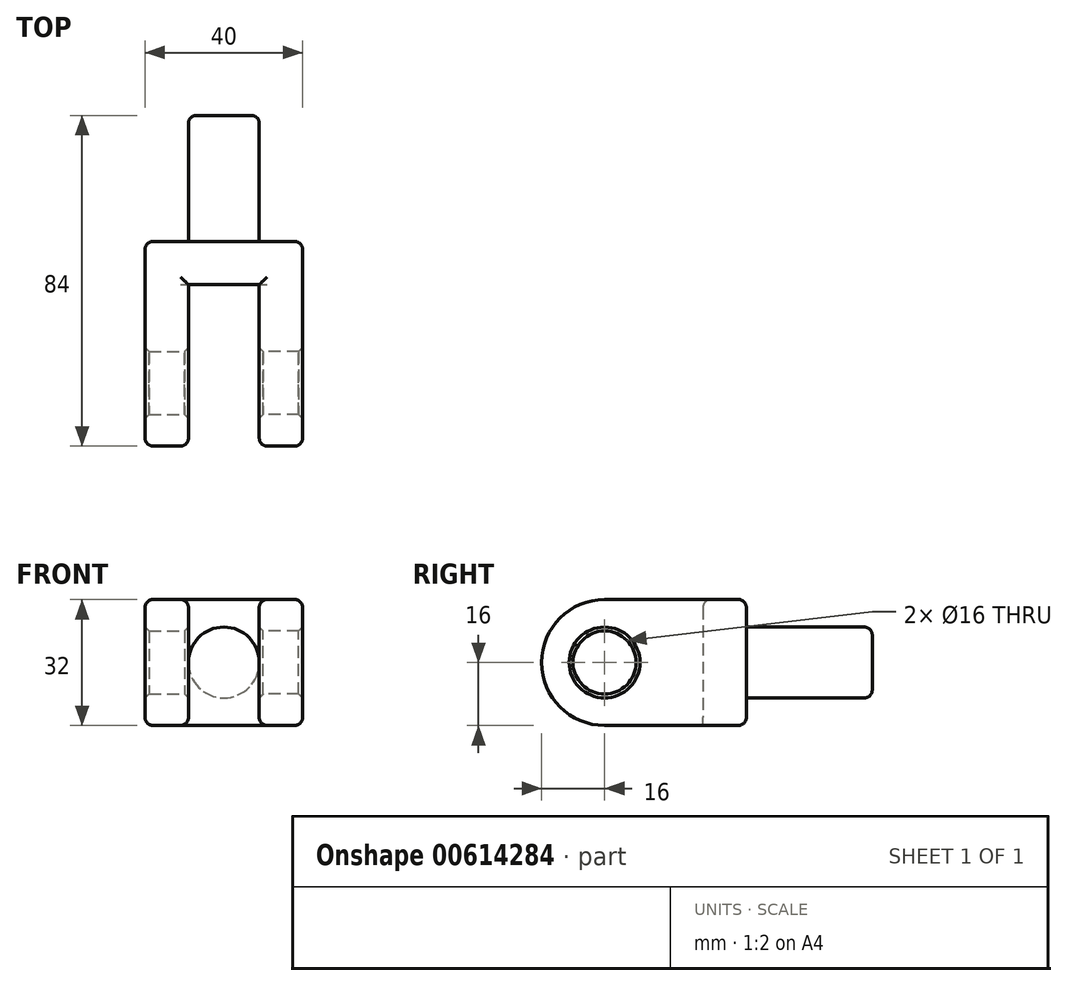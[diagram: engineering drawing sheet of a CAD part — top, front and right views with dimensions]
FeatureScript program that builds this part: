
annotation { "Feature Type Name" : "Feature", "Feature Type Description" : "" }
export const myFeature = defineFeature(function(context is Context, id is Id, definition is map)
    precondition{}
    {
        {
            var Q0;
            Q0=qCreatedBy(makeId("Front.planeOp"),FACE);
            var sketch = newSketch(context, id + "F0", { "sketchPlane" : qUnion([Q0])});
            skLineSegment(sketch, "E0.bottom", {"start": v(-9, 16) * mm, "end": v(9, 16) * mm});
            skLineSegment(sketch, "E0.top", {"start": v(-9, -16) * mm, "end": v(9, -16) * mm});
            skLineSegment(sketch, "E0.left", {"start": v(-9, 16) * mm, "end": v(-9, -16) * mm});
            skLineSegment(sketch, "E0.right", {"start": v(9, 16) * mm, "end": v(9, -16) * mm});
            skSolve(sketch);
        }
        {
            var Q0;
            Q0 = qSketchRegion(id + "F0", true);
            extrude(context, id + "F1", {"entities" : qUnion([Q0]), "depth" : 11 * mm, "offsetDistance" : 25 * mm});
        }
        {
            var Q0;
            Q0=makeQuery(id+"F1.opExtrude","SWEPT_FACE",FACE,{"disambiguationData":[OSD([sQuery(id+"F0.wireOp",EDGE,"E0.right")])]});
            var sketch = newSketch(context, id + "F2", { "sketchPlane" : qUnion([Q0])});
            skLineSegment(sketch, "E1", {"start": v(0, -16) * mm, "end": v(0, 16) * mm});
            skLineSegment(sketch, "E2", {"start": v(0, 16) * mm, "end": v(-36, 16) * mm});
            skPoint(sketch, "E2.endSnap0", {"position": v(-5.5, 16) * mm});
            skLineSegment(sketch, "E3", {"start": v(0, -16) * mm, "end": v(-36, -16) * mm});
            skArc(sketch, "E4", {"start": v(-36, 16) * mm, "mid": v(-52, 0) * mm, "end": v(-36, -16) * mm});
            skCircle(sketch, "E5", {"center": v(-36, 0) * mm, "radius": 8 * mm});
            skSolve(sketch);
        }
        {
            var Q0;
            Q0 = qSketchRegion(id + "F2", true);
            extrude(context, id + "F3", {"entities" : qUnion([Q0]), "operationType" : NewBodyOperationType.ADD, "depth" : 11 * mm, "offsetDistance" : 25 * mm});
        }
        {
            var Q0;
            Q0=makeQuery(id+"F1.opExtrude","SWEPT_BODY",BODY,{"disambiguationData":[OSD([sQuery(id+"F0.wireOp",EDGE,"E0.bottom"),sQuery(id+"F0.wireOp",EDGE,"E0.top"),sQuery(id+"F0.wireOp",EDGE,"E0.left"),sQuery(id+"F0.wireOp",EDGE,"E0.right")])]});
            var Q1;
            Q1=qCreatedBy(makeId("Right.planeOp"),FACE);
            mirror(context, id + "F4", {"operationType" : NewBodyOperationType.ADD, "entities" : qUnion([Q0]), "mirrorPlane" : qUnion([Q1])});
        }
        {
            var Q0;
            {var subQ0=makeQuery(id+"F3.boolean.opBoolean","MERGE",FACE,{"derivedFrom":[makeQuery(id+"F1.opExtrude","CAP_FACE",FACE,{"disambiguationData":[OSD([sQuery(id+"F0.wireOp",EDGE,"E0.bottom"),sQuery(id+"F0.wireOp",EDGE,"E0.top"),sQuery(id+"F0.wireOp",EDGE,"E0.left"),sQuery(id+"F0.wireOp",EDGE,"E0.right")])],"isStart":true}),makeQuery(id+"F3.opExtrude","SWEPT_FACE",FACE,{"disambiguationData":[OSD([sQuery(id+"F2.wireOp",EDGE,"E1")])]})]});Q0=makeQuery(id+"F4.boolean.opBoolean","MERGE",FACE,{"derivedFrom":[subQ0,makeQuery(id+"F4.opPattern","COPY",FACE,{"derivedFrom":subQ0,"instanceName":"1"})]});}
            var sketch = newSketch(context, id + "F5", { "sketchPlane" : qUnion([Q0])});
            skCircle(sketch, "E6", {"center": v(0, 0) * mm, "radius": 9 * mm});
            skSolve(sketch);
        }
        {
            var Q0;
            Q0=makeQuery(id+"F5.imprint","IMPRINT",FACE,{"disambiguationData":[TD([[makeQuery(id+"F5.imprint","IMPRINT",EDGE,{"derivedFrom":sQuery(id+"F5.wireOp",EDGE,"E6")}),1.0]])]});
            extrude(context, id + "F6", {"entities" : qUnion([Q0]), "operationType" : NewBodyOperationType.ADD, "depth" : 32 * mm, "offsetDistance" : 25 * mm});
        }
        {
            var Q0;
            Q0=makeQuery(id+"F3.opExtrude","CAP_EDGE",EDGE,{"disambiguationData":[OSD([sQuery(id+"F2.wireOp",EDGE,"E5")])],"isStart":true});
            var Q1;
            Q1=makeQuery(id+"F3.opExtrude","CAP_EDGE",EDGE,{"disambiguationData":[OSD([sQuery(id+"F2.wireOp",EDGE,"E5")])],"isStart":false});
            var Q2;
            Q2=makeQuery(id+"F4.opPattern","COPY",EDGE,{"derivedFrom":makeQuery(id+"F3.opExtrude","CAP_EDGE",EDGE,{"disambiguationData":[OSD([sQuery(id+"F2.wireOp",EDGE,"E5")])],"isStart":true}),"instanceName":"1"});
            var Q3;
            Q3=makeQuery(id+"F4.opPattern","COPY",EDGE,{"derivedFrom":makeQuery(id+"F3.opExtrude","CAP_EDGE",EDGE,{"disambiguationData":[OSD([sQuery(id+"F2.wireOp",EDGE,"E5")])],"isStart":false}),"instanceName":"1"});
            chamfer(context, id + "F7", {"entities" : qUnion([Q0, Q1, Q2, Q3]), "width" : 1 * mm, "tangentPropagation" : true});
        }
        {
            var Q0;
            {var subQ0=makeQuery(id+"F3.boolean.opBoolean","MERGE",FACE,{"derivedFrom":[makeQuery(id+"F1.opExtrude","SWEPT_FACE",FACE,{"disambiguationData":[OSD([sQuery(id+"F0.wireOp",EDGE,"E0.bottom")])]}),makeQuery(id+"F3.opExtrude","SWEPT_FACE",FACE,{"disambiguationData":[OSD([sQuery(id+"F2.wireOp",EDGE,"E2")])]})]});Q0=makeQuery(id+"F4.boolean.opBoolean","MERGE",FACE,{"derivedFrom":[subQ0,makeQuery(id+"F4.opPattern","COPY",FACE,{"derivedFrom":subQ0,"instanceName":"1"})]});}
            var Q1;
            Q1=makeQuery(id+"F3.opExtrude","CAP_EDGE",EDGE,{"disambiguationData":[OSD([sQuery(id+"F2.wireOp",EDGE,"E1")])],"isStart":false});
            var Q2;
            {var subQ0=makeQuery(id+"F3.boolean.opBoolean","MERGE",EDGE,{"derivedFrom":[makeQuery(id+"F1.opExtrude","CAP_EDGE",EDGE,{"disambiguationData":[OSD([sQuery(id+"F0.wireOp",EDGE,"E0.top")])],"isStart":true}),makeQuery(id+"F3.opExtrude","SWEPT_EDGE",EDGE,{"disambiguationData":[OSD([sQuery(id+"F2.wireOp",EDGE,"E1"),sQuery(id+"F2.wireOp",EDGE,"E3")])]})]});Q2=makeQuery(id+"F4.boolean.opBoolean","MERGE",EDGE,{"derivedFrom":[subQ0,makeQuery(id+"F4.opPattern","COPY",EDGE,{"derivedFrom":subQ0,"instanceName":"1"})]});}
            var Q3;
            Q3=makeQuery(id+"F4.opPattern","COPY",EDGE,{"derivedFrom":makeQuery(id+"F3.opExtrude","CAP_EDGE",EDGE,{"disambiguationData":[OSD([sQuery(id+"F2.wireOp",EDGE,"E1")])],"isStart":false}),"instanceName":"1"});
            var Q4;
            Q4=makeQuery(id+"F6.opExtrude","CAP_EDGE",EDGE,{"disambiguationData":[OSD([sQuery(id+"F5.wireOp",EDGE,"E6")])],"isStart":false});
            fillet(context, id + "F8", {"entities" : qUnion([Q0, Q1, Q2, Q3, Q4]), "radius" : 2 * mm, "tangentPropagation" : true, "allowEdgeOverflow" : false});
        }
    });
